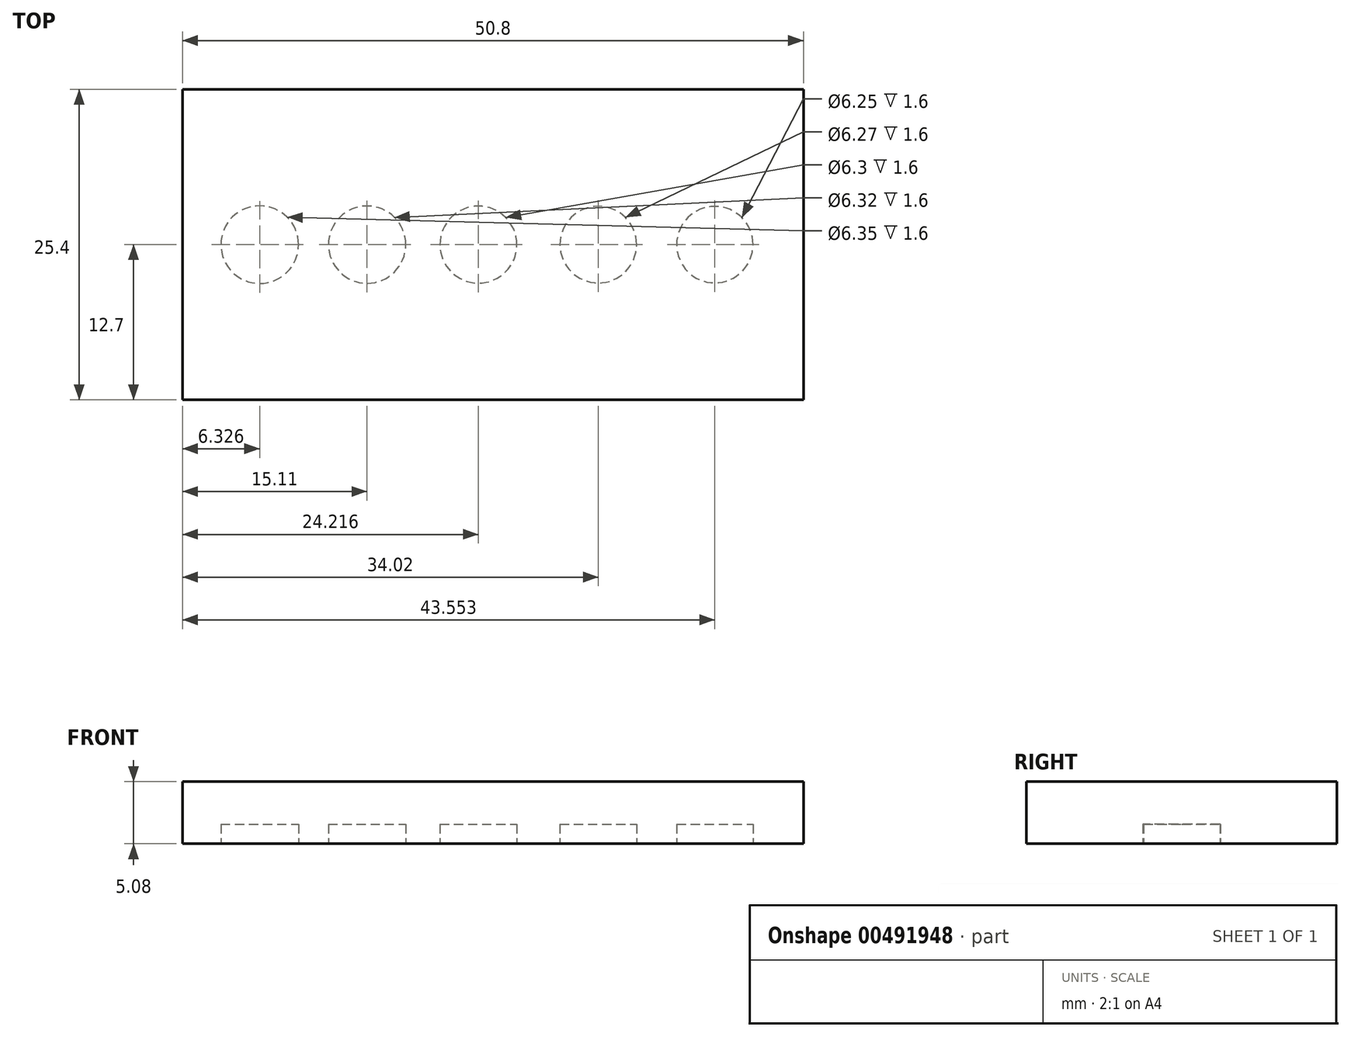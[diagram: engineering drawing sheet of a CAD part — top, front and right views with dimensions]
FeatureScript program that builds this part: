
annotation { "Feature Type Name" : "Feature", "Feature Type Description" : "" }
export const myFeature = defineFeature(function(context is Context, id is Id, definition is map)
    precondition{}
    {
        {
            var Q0;
            Q0=qCreatedBy(makeId("Top.planeOp"),FACE);
            var sketch = newSketch(context, id + "F0", { "sketchPlane" : qUnion([Q0])});
            skLineSegment(sketch, "E0.bottom", {"start": v(25.4, 12.7) * mm, "end": v(-25.4, 12.7) * mm});
            skLineSegment(sketch, "E0.top", {"start": v(25.4, -12.7) * mm, "end": v(-25.4, -12.7) * mm});
            skLineSegment(sketch, "E0.left", {"start": v(25.4, 12.7) * mm, "end": v(25.4, -12.7) * mm});
            skLineSegment(sketch, "E0.right", {"start": v(-25.4, 12.7) * mm, "end": v(-25.4, -12.7) * mm});
            skPoint(sketch, "E0.middle", {"position": v(0, 0) * mm});
            skSolve(sketch);
        }
        {
            var Q0;
            Q0 = qSketchRegion(id + "F0", true);
            extrude(context, id + "F1", {"entities" : qUnion([Q0]), "depth" : 5.08 * mm});
        }
        {
            var Q0;
            Q0=makeQuery(id+"F1.opExtrude","CAP_FACE",FACE,{"disambiguationData":[OSD([sQuery(id+"F0.wireOp",EDGE,"E0.bottom"),sQuery(id+"F0.wireOp",EDGE,"E0.top"),sQuery(id+"F0.wireOp",EDGE,"E0.left"),sQuery(id+"F0.wireOp",EDGE,"E0.right")])],"isStart":true});
            var sketch = newSketch(context, id + "F2", { "sketchPlane" : qUnion([Q0])});
            skCircle(sketch, "E1", {"center": v(-19.07, 0) * mm, "radius": 3.18 * mm});
            skCircle(sketch, "E2", {"center": v(-10.29, 0) * mm, "radius": 3.16 * mm});
            skCircle(sketch, "E3", {"center": v(-1.18, 0) * mm, "radius": 3.15 * mm});
            skCircle(sketch, "E4", {"center": v(8.62, 0) * mm, "radius": 3.14 * mm});
            skCircle(sketch, "E5", {"center": v(18.15, 0) * mm, "radius": 3.12 * mm});
            skSolve(sketch);
        }
        {
            var Q0;
            Q0 = qSketchRegion(id + "F2", true);
            extrude(context, id + "F3", {"entities" : qUnion([Q0]), "operationType" : NewBodyOperationType.REMOVE, "oppositeDirection" : true, "depth" : 1.6 * mm});
        }
    });
